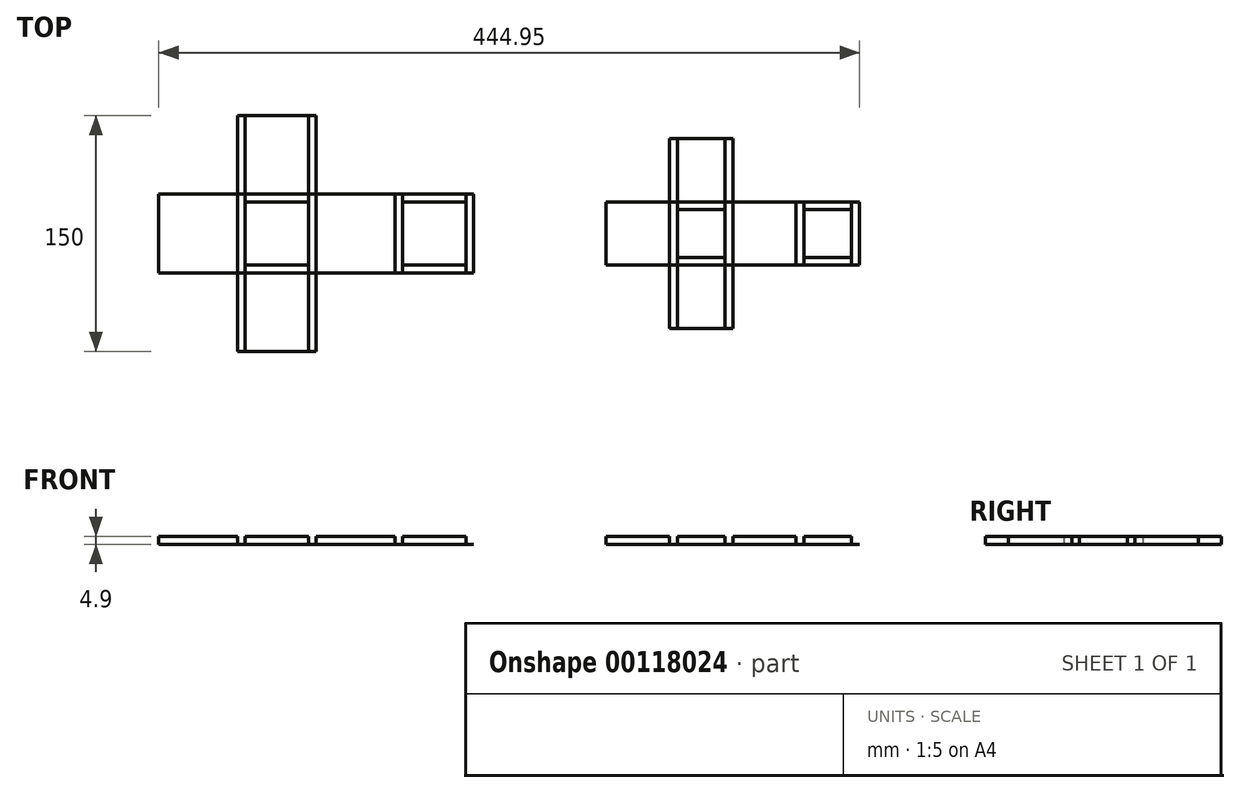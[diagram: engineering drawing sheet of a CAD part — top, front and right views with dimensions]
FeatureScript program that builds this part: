
annotation { "Feature Type Name" : "Feature", "Feature Type Description" : "" }
export const myFeature = defineFeature(function(context is Context, id is Id, definition is map)
    precondition{}
    {
        {
            assignVariable(context, id + "F0", {"name" : "foam_w", "anyValue" : 4.9 * mm});
        }
        {
            var Q0;
            Q0=qCreatedBy(makeId("Top.planeOp"),FACE);
            var sketch = newSketch(context, id + "F1", { "sketchPlane" : qUnion([Q0])});
            skLineSegment(sketch, "E0.bottom", {"start": v(25, -25) * mm, "end": v(-25, -25) * mm});
            skLineSegment(sketch, "E0.top", {"start": v(25, 25) * mm, "end": v(-25, 25) * mm});
            skLineSegment(sketch, "E0.left", {"start": v(25, -25) * mm, "end": v(25, 25) * mm});
            skLineSegment(sketch, "E0.right", {"start": v(-25, -25) * mm, "end": v(-25, 25) * mm});
            skPoint(sketch, "E0.middle", {"position": v(0, 0) * mm});
            skLineSegment(sketch, "E1.bottom", {"start": v(20.1, 20.1) * mm, "end": v(-20.1, 20.1) * mm});
            skLineSegment(sketch, "E1.top", {"start": v(20.1, -20.1) * mm, "end": v(-20.1, -20.1) * mm});
            skLineSegment(sketch, "E1.left", {"start": v(20.1, 20.1) * mm, "end": v(20.1, -20.1) * mm});
            skLineSegment(sketch, "E1.right", {"start": v(-20.1, 20.1) * mm, "end": v(-20.1, -20.1) * mm});
            skLineSegment(sketch, "E2", {"start": v(25, 25) * mm, "end": v(75, 25) * mm});
            skLineSegment(sketch, "E3", {"start": v(75, 25) * mm, "end": v(75, -25) * mm});
            skLineSegment(sketch, "E4", {"start": v(75, -25) * mm, "end": v(25, -25) * mm});
            skLineSegment(sketch, "E5", {"start": v(-25, 25) * mm, "end": v(-75, 25) * mm});
            skLineSegment(sketch, "E6", {"start": v(-75, 25) * mm, "end": v(-75, -25) * mm});
            skLineSegment(sketch, "E7", {"start": v(-75, -25) * mm, "end": v(-25, -25) * mm});
            skLineSegment(sketch, "E8", {"start": v(-25, 25) * mm, "end": v(-25, 75) * mm});
            skLineSegment(sketch, "E9", {"start": v(-25, 75) * mm, "end": v(25, 75) * mm});
            skLineSegment(sketch, "E10", {"start": v(25, 75) * mm, "end": v(25, 25) * mm});
            skLineSegment(sketch, "E11", {"start": v(-25, -25) * mm, "end": v(-25, -75) * mm});
            skLineSegment(sketch, "E12", {"start": v(-25, -75) * mm, "end": v(25, -75) * mm});
            skLineSegment(sketch, "E13", {"start": v(25, -75) * mm, "end": v(25, -25) * mm});
            skLineSegment(sketch, "E14", {"start": v(-20.1, 75) * mm, "end": v(-20.1, 25) * mm});
            skLineSegment(sketch, "E15", {"start": v(20.1, 75) * mm, "end": v(20.1, 25) * mm});
            skLineSegment(sketch, "E16", {"start": v(-20.1, -25) * mm, "end": v(-20.1, -75) * mm});
            skLineSegment(sketch, "E17", {"start": v(20.1, -25) * mm, "end": v(20.1, -75) * mm});
            skLineSegment(sketch, "E18", {"start": v(-20.1, 25) * mm, "end": v(-20.1, 20.1) * mm});
            skLineSegment(sketch, "E19", {"start": v(-20.1, -20.1) * mm, "end": v(-20.1, -25) * mm});
            skLineSegment(sketch, "E20", {"start": v(20.1, -20.1) * mm, "end": v(20.1, -25) * mm});
            skLineSegment(sketch, "E21", {"start": v(20.1, 25) * mm, "end": v(20.1, 20.1) * mm});
            skLineSegment(sketch, "E22", {"start": v(75, 25) * mm, "end": v(125, 25) * mm});
            skLineSegment(sketch, "E23", {"start": v(125, 25) * mm, "end": v(125, -25) * mm});
            skLineSegment(sketch, "E24", {"start": v(125, -25) * mm, "end": v(75, -25) * mm});
            skLineSegment(sketch, "E25.bottom", {"start": v(120.1, -20.1) * mm, "end": v(79.9, -20.1) * mm});
            skLineSegment(sketch, "E25.top", {"start": v(120.1, 20.1) * mm, "end": v(79.9, 20.1) * mm});
            skLineSegment(sketch, "E25.left", {"start": v(120.1, -20.1) * mm, "end": v(120.1, 20.1) * mm});
            skLineSegment(sketch, "E25.right", {"start": v(79.9, -20.1) * mm, "end": v(79.9, 20.1) * mm});
            skPoint(sketch, "E25.middle", {"position": v(100, 0) * mm});
            skLineSegment(sketch, "E26", {"start": v(75, -25) * mm, "end": v(125, 25) * mm, "construction": true});
            skLineSegment(sketch, "E27", {"start": v(79.9, 25) * mm, "end": v(79.9, -25) * mm});
            skLineSegment(sketch, "E28", {"start": v(120.1, 25) * mm, "end": v(120.1, -25) * mm});
            skSolve(sketch);
        }
        {
            var Q0;
            Q0=qCreatedBy(makeId("Top.planeOp"),FACE);
            var sketch = newSketch(context, id + "F2", { "sketchPlane" : qUnion([Q0])});
            skLineSegment(sketch, "E29.bottom", {"start": v(289.55, -20.1) * mm, "end": v(249.35, -20.1) * mm});
            skLineSegment(sketch, "E29.top", {"start": v(289.55, 20.1) * mm, "end": v(249.35, 20.1) * mm});
            skLineSegment(sketch, "E29.left", {"start": v(289.55, -20.1) * mm, "end": v(289.55, 20.1) * mm});
            skLineSegment(sketch, "E29.right", {"start": v(249.35, -20.1) * mm, "end": v(249.35, 20.1) * mm});
            skPoint(sketch, "E29.middle", {"position": v(269.45, 0) * mm});
            skLineSegment(sketch, "E30.bottom", {"start": v(284.65, 15.2) * mm, "end": v(254.25, 15.2) * mm});
            skLineSegment(sketch, "E30.top", {"start": v(284.65, -15.2) * mm, "end": v(254.25, -15.2) * mm});
            skLineSegment(sketch, "E30.left", {"start": v(284.65, 15.2) * mm, "end": v(284.65, -15.2) * mm});
            skLineSegment(sketch, "E30.right", {"start": v(254.25, 15.2) * mm, "end": v(254.25, -15.2) * mm});
            skLineSegment(sketch, "E31", {"start": v(289.55, 20.1) * mm, "end": v(329.75, 20.1) * mm});
            skLineSegment(sketch, "E32", {"start": v(329.75, 20.1) * mm, "end": v(329.75, -20.1) * mm});
            skLineSegment(sketch, "E33", {"start": v(329.75, -20.1) * mm, "end": v(289.55, -20.1) * mm});
            skLineSegment(sketch, "E34", {"start": v(249.35, 20.1) * mm, "end": v(209.15, 20.1) * mm});
            skLineSegment(sketch, "E35", {"start": v(209.15, 20.1) * mm, "end": v(209.15, -20.1) * mm});
            skLineSegment(sketch, "E36", {"start": v(209.15, -20.1) * mm, "end": v(249.35, -20.1) * mm});
            skLineSegment(sketch, "E37", {"start": v(249.35, 20.1) * mm, "end": v(249.35, 60.3) * mm});
            skLineSegment(sketch, "E38", {"start": v(249.35, 60.3) * mm, "end": v(289.55, 60.3) * mm});
            skLineSegment(sketch, "E39", {"start": v(289.55, 60.3) * mm, "end": v(289.55, 20.1) * mm});
            skLineSegment(sketch, "E40", {"start": v(249.35, -20.1) * mm, "end": v(249.35, -60.3) * mm});
            skLineSegment(sketch, "E41", {"start": v(249.35, -60.3) * mm, "end": v(289.55, -60.3) * mm});
            skLineSegment(sketch, "E42", {"start": v(289.55, -60.3) * mm, "end": v(289.55, -20.1) * mm});
            skLineSegment(sketch, "E43", {"start": v(254.25, 60.3) * mm, "end": v(254.25, 20.1) * mm});
            skLineSegment(sketch, "E44", {"start": v(284.65, 60.3) * mm, "end": v(284.65, 20.1) * mm});
            skLineSegment(sketch, "E45", {"start": v(254.25, -20.1) * mm, "end": v(254.25, -60.3) * mm});
            skLineSegment(sketch, "E46", {"start": v(284.65, -20.1) * mm, "end": v(284.65, -60.3) * mm});
            skLineSegment(sketch, "E47", {"start": v(254.25, 20.1) * mm, "end": v(254.25, 15.2) * mm});
            skLineSegment(sketch, "E48", {"start": v(254.25, -15.2) * mm, "end": v(254.25, -20.1) * mm});
            skLineSegment(sketch, "E49", {"start": v(284.65, -15.2) * mm, "end": v(284.65, -20.1) * mm});
            skLineSegment(sketch, "E50", {"start": v(284.65, 20.1) * mm, "end": v(284.65, 15.2) * mm});
            skLineSegment(sketch, "E51", {"start": v(329.75, 20.1) * mm, "end": v(369.95, 20.1) * mm});
            skLineSegment(sketch, "E52", {"start": v(369.95, 20.1) * mm, "end": v(369.95, -20.1) * mm});
            skLineSegment(sketch, "E53", {"start": v(369.95, -20.1) * mm, "end": v(329.75, -20.1) * mm});
            skLineSegment(sketch, "E54.bottom", {"start": v(365.05, -15.2) * mm, "end": v(334.65, -15.2) * mm});
            skLineSegment(sketch, "E54.top", {"start": v(365.05, 15.2) * mm, "end": v(334.65, 15.2) * mm});
            skLineSegment(sketch, "E54.left", {"start": v(365.05, -15.2) * mm, "end": v(365.05, 15.2) * mm});
            skLineSegment(sketch, "E54.right", {"start": v(334.65, -15.2) * mm, "end": v(334.65, 15.2) * mm});
            skPoint(sketch, "E54.middle", {"position": v(349.85, 0) * mm});
            skLineSegment(sketch, "E55", {"start": v(329.75, -20.1) * mm, "end": v(369.95, 20.1) * mm, "construction": true});
            skLineSegment(sketch, "E56", {"start": v(334.65, 20.1) * mm, "end": v(334.65, -20.1) * mm});
            skLineSegment(sketch, "E57", {"start": v(365.05, 20.1) * mm, "end": v(365.05, -20.1) * mm});
            skSolve(sketch);
        }
        {
            var Q0;
            Q0=makeQuery(id+"F1.imprint","IMPRINT",FACE,{"disambiguationData":[TD([[makeQuery(id+"F1.imprint","IMPRINT",EDGE,{"derivedFrom":sQuery(id+"F1.wireOp",EDGE,"E0.right")}),1.0]])]});
            var Q1;
            Q1=makeQuery(id+"F1.imprint","IMPRINT",FACE,{"disambiguationData":[TD([[makeQuery(id+"F1.imprint","IMPRINT",EDGE,{"derivedFrom":sQuery(id+"F1.wireOp",EDGE,"E1.bottom")}),1.0]])]});
            var Q2;
            {var subQ0=sQuery(id+"F1.wireOp",EDGE,"E14");Q2=makeQuery(id+"F1.imprint","IMPRINT",FACE,{"disambiguationData":[TD([[makeQuery(id+"F1.imprint","IMPRINT",EDGE,{"derivedFrom":subQ0}),1.0]])]});}
            var Q3;
            {var subQ0=sQuery(id+"F1.wireOp",EDGE,"E16");Q3=makeQuery(id+"F1.imprint","IMPRINT",FACE,{"disambiguationData":[TD([[makeQuery(id+"F1.imprint","IMPRINT",EDGE,{"derivedFrom":subQ0}),1.0]])]});}
            var Q4;
            Q4=makeQuery(id+"F1.imprint","IMPRINT",FACE,{"disambiguationData":[TD([[makeQuery(id+"F1.imprint","IMPRINT",EDGE,{"derivedFrom":sQuery(id+"F1.wireOp",EDGE,"E0.left")}),-1.0]])]});
            var Q5;
            {var subQ0=sQuery(id+"F1.wireOp",EDGE,"E25.bottom");Q5=makeQuery(id+"F1.imprint","IMPRINT",FACE,{"disambiguationData":[TD([[makeQuery(id+"F1.imprint","IMPRINT",EDGE,{"derivedFrom":subQ0}),-1.0]])]});}
            var Q6;
            {var subQ0=sQuery(id+"F2.wireOp",EDGE,"E43");Q6=makeQuery(id+"F2.imprint","IMPRINT",FACE,{"disambiguationData":[TD([[makeQuery(id+"F2.imprint","IMPRINT",EDGE,{"derivedFrom":subQ0}),1.0]])]});}
            var Q7;
            {var subQ0=sQuery(id+"F2.wireOp",EDGE,"E45");Q7=makeQuery(id+"F2.imprint","IMPRINT",FACE,{"disambiguationData":[TD([[makeQuery(id+"F2.imprint","IMPRINT",EDGE,{"derivedFrom":subQ0}),1.0]])]});}
            var Q8;
            Q8=makeQuery(id+"F2.imprint","IMPRINT",FACE,{"disambiguationData":[TD([[makeQuery(id+"F2.imprint","IMPRINT",EDGE,{"derivedFrom":sQuery(id+"F2.wireOp",EDGE,"E29.right")}),1.0]])]});
            var Q9;
            Q9=makeQuery(id+"F2.imprint","IMPRINT",FACE,{"disambiguationData":[TD([[makeQuery(id+"F2.imprint","IMPRINT",EDGE,{"derivedFrom":sQuery(id+"F2.wireOp",EDGE,"E29.left")}),-1.0]])]});
            var Q10;
            {var subQ0=sQuery(id+"F2.wireOp",EDGE,"E54.bottom");Q10=makeQuery(id+"F2.imprint","IMPRINT",FACE,{"disambiguationData":[TD([[makeQuery(id+"F2.imprint","IMPRINT",EDGE,{"derivedFrom":subQ0}),-1.0]])]});}
            var Q11;
            Q11=makeQuery(id+"F2.imprint","IMPRINT",FACE,{"disambiguationData":[TD([[makeQuery(id+"F2.imprint","IMPRINT",EDGE,{"derivedFrom":sQuery(id+"F2.wireOp",EDGE,"E30.bottom")}),1.0]])]});
            extrude(context, id + "F3", {"entities" : qUnion([Q0, Q1, Q2, Q3, Q4, Q5, Q6, Q7, Q8, Q9, Q10, Q11]), "depth" : getVariable(context, 'foam_w')});
        }
        {
            var Q0;
            {var subQ0=sQuery(id+"F1.wireOp",EDGE,"E8");Q0=makeQuery(id+"F1.imprint","IMPRINT",FACE,{"disambiguationData":[TD([[makeQuery(id+"F1.imprint","IMPRINT",EDGE,{"derivedFrom":subQ0}),-1.0]])]});}
            var Q1;
            Q1=makeQuery(id+"F1.imprint","IMPRINT",FACE,{"disambiguationData":[TD([[makeQuery(id+"F1.imprint","IMPRINT",EDGE,{"derivedFrom":sQuery(id+"F1.wireOp",EDGE,"E1.bottom")}),-1.0]])]});
            var Q2;
            Q2=makeQuery(id+"F1.imprint","IMPRINT",FACE,{"disambiguationData":[TD([[makeQuery(id+"F1.imprint","IMPRINT",EDGE,{"derivedFrom":sQuery(id+"F1.wireOp",EDGE,"E1.top")}),1.0]])]});
            var Q3;
            {var subQ0=sQuery(id+"F1.wireOp",EDGE,"E10");Q3=makeQuery(id+"F1.imprint","IMPRINT",FACE,{"disambiguationData":[TD([[makeQuery(id+"F1.imprint","IMPRINT",EDGE,{"derivedFrom":subQ0}),-1.0]])]});}
            var Q4;
            {var subQ0=sQuery(id+"F1.wireOp",EDGE,"E13");Q4=makeQuery(id+"F1.imprint","IMPRINT",FACE,{"disambiguationData":[TD([[makeQuery(id+"F1.imprint","IMPRINT",EDGE,{"derivedFrom":subQ0}),1.0]])]});}
            var Q5;
            {var subQ0=sQuery(id+"F1.wireOp",EDGE,"E11");Q5=makeQuery(id+"F1.imprint","IMPRINT",FACE,{"disambiguationData":[TD([[makeQuery(id+"F1.imprint","IMPRINT",EDGE,{"derivedFrom":subQ0}),1.0]])]});}
            var Q6;
            {var subQ5=sQuery(id+"F1.wireOp",EDGE,"E25.top");Q6=makeQuery(id+"F1.imprint","IMPRINT",FACE,{"disambiguationData":[TD([[makeQuery(id+"F1.imprint","IMPRINT",EDGE,{"derivedFrom":subQ5}),-1.0]])]});}
            var Q7;
            {var subQ5=sQuery(id+"F1.wireOp",EDGE,"E25.bottom");Q7=makeQuery(id+"F1.imprint","IMPRINT",FACE,{"disambiguationData":[TD([[makeQuery(id+"F1.imprint","IMPRINT",EDGE,{"derivedFrom":subQ5}),1.0]])]});}
            var Q8;
            {var subQ0=sQuery(id+"F2.wireOp",EDGE,"E37");Q8=makeQuery(id+"F2.imprint","IMPRINT",FACE,{"disambiguationData":[TD([[makeQuery(id+"F2.imprint","IMPRINT",EDGE,{"derivedFrom":subQ0}),-1.0]])]});}
            var Q9;
            {var subQ0=sQuery(id+"F2.wireOp",EDGE,"E39");Q9=makeQuery(id+"F2.imprint","IMPRINT",FACE,{"disambiguationData":[TD([[makeQuery(id+"F2.imprint","IMPRINT",EDGE,{"derivedFrom":subQ0}),-1.0]])]});}
            var Q10;
            Q10=makeQuery(id+"F2.imprint","IMPRINT",FACE,{"disambiguationData":[TD([[makeQuery(id+"F2.imprint","IMPRINT",EDGE,{"derivedFrom":sQuery(id+"F2.wireOp",EDGE,"E30.bottom")}),-1.0]])]});
            var Q11;
            {var subQ0=sQuery(id+"F2.wireOp",EDGE,"E40");Q11=makeQuery(id+"F2.imprint","IMPRINT",FACE,{"disambiguationData":[TD([[makeQuery(id+"F2.imprint","IMPRINT",EDGE,{"derivedFrom":subQ0}),1.0]])]});}
            var Q12;
            Q12=makeQuery(id+"F2.imprint","IMPRINT",FACE,{"disambiguationData":[TD([[makeQuery(id+"F2.imprint","IMPRINT",EDGE,{"derivedFrom":sQuery(id+"F2.wireOp",EDGE,"E30.top")}),1.0]])]});
            var Q13;
            {var subQ0=sQuery(id+"F2.wireOp",EDGE,"E42");Q13=makeQuery(id+"F2.imprint","IMPRINT",FACE,{"disambiguationData":[TD([[makeQuery(id+"F2.imprint","IMPRINT",EDGE,{"derivedFrom":subQ0}),1.0]])]});}
            var Q14;
            {var subQ5=sQuery(id+"F2.wireOp",EDGE,"E54.top");Q14=makeQuery(id+"F2.imprint","IMPRINT",FACE,{"disambiguationData":[TD([[makeQuery(id+"F2.imprint","IMPRINT",EDGE,{"derivedFrom":subQ5}),-1.0]])]});}
            var Q15;
            {var subQ5=sQuery(id+"F2.wireOp",EDGE,"E54.bottom");Q15=makeQuery(id+"F2.imprint","IMPRINT",FACE,{"disambiguationData":[TD([[makeQuery(id+"F2.imprint","IMPRINT",EDGE,{"derivedFrom":subQ5}),1.0]])]});}
            extrude(context, id + "F4", {"entities" : qUnion([Q0, Q1, Q2, Q3, Q4, Q5, Q6, Q7, Q8, Q9, Q10, Q11, Q12, Q13, Q14, Q15]), "depth" : 0.1 * mm});
        }
        {
            var Q0;
            {var subQ0=sQuery(id+"F1.wireOp",EDGE,"E0.right");Q0=makeQuery(id+"F1.imprint","IMPRINT",FACE,{"disambiguationData":[TD([[makeQuery(id+"F1.imprint","IMPRINT",EDGE,{"derivedFrom":subQ0}),-1.0]])]});}
            var Q1;
            {var subQ0=sQuery(id+"F1.wireOp",EDGE,"E0.left");Q1=makeQuery(id+"F1.imprint","IMPRINT",FACE,{"disambiguationData":[TD([[makeQuery(id+"F1.imprint","IMPRINT",EDGE,{"derivedFrom":subQ0}),1.0]])]});}
            var Q2;
            {var subQ1=sQuery(id+"F1.wireOp",EDGE,"E3");Q2=makeQuery(id+"F1.imprint","IMPRINT",FACE,{"disambiguationData":[TD([[makeQuery(id+"F1.imprint","IMPRINT",EDGE,{"derivedFrom":subQ1}),1.0]])]});}
            var Q3;
            {var subQ1=sQuery(id+"F1.wireOp",EDGE,"E23");Q3=makeQuery(id+"F1.imprint","IMPRINT",FACE,{"disambiguationData":[TD([[makeQuery(id+"F1.imprint","IMPRINT",EDGE,{"derivedFrom":subQ1}),-1.0]])]});}
            var Q4;
            {var subQ0=sQuery(id+"F2.wireOp",EDGE,"E29.right");Q4=makeQuery(id+"F2.imprint","IMPRINT",FACE,{"disambiguationData":[TD([[makeQuery(id+"F2.imprint","IMPRINT",EDGE,{"derivedFrom":subQ0}),-1.0]])]});}
            var Q5;
            {var subQ0=sQuery(id+"F2.wireOp",EDGE,"E29.left");Q5=makeQuery(id+"F2.imprint","IMPRINT",FACE,{"disambiguationData":[TD([[makeQuery(id+"F2.imprint","IMPRINT",EDGE,{"derivedFrom":subQ0}),1.0]])]});}
            var Q6;
            {var subQ5=sQuery(id+"F2.wireOp",EDGE,"E32");Q6=makeQuery(id+"F2.imprint","IMPRINT",FACE,{"disambiguationData":[TD([[makeQuery(id+"F2.imprint","IMPRINT",EDGE,{"derivedFrom":subQ5}),1.0]])]});}
            var Q7;
            {var subQ1=sQuery(id+"F2.wireOp",EDGE,"E52");Q7=makeQuery(id+"F2.imprint","IMPRINT",FACE,{"disambiguationData":[TD([[makeQuery(id+"F2.imprint","IMPRINT",EDGE,{"derivedFrom":subQ1}),-1.0]])]});}
            extrude(context, id + "F5", {"entities" : qUnion([Q0, Q1, Q2, Q3, Q4, Q5, Q6, Q7]), "depth" : 0.1 * mm});
        }
    });
